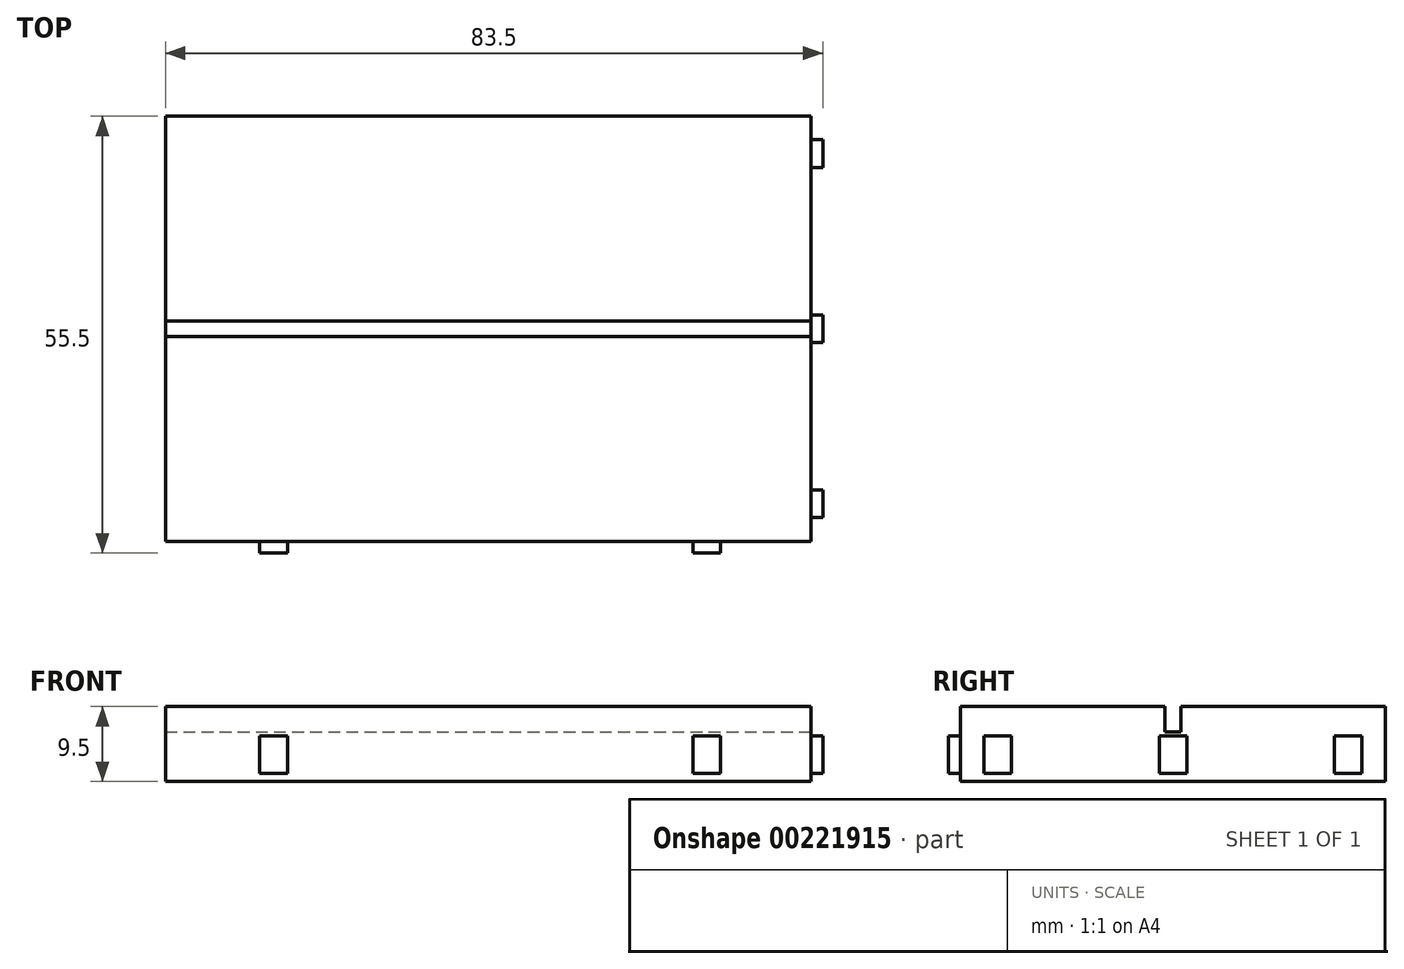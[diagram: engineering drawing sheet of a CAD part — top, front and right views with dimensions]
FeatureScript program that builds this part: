
annotation { "Feature Type Name" : "Feature", "Feature Type Description" : "" }
export const myFeature = defineFeature(function(context is Context, id is Id, definition is map)
    precondition{}
    {
        {
            var Q0;
            Q0=qCreatedBy(makeId("Top.planeOp"),FACE);
            var sketch = newSketch(context, id + "F0", { "sketchPlane" : qUnion([Q0])});
            skLineSegment(sketch, "E0.bottom", {"start": v(41, -27) * mm, "end": v(-41, -27) * mm});
            skLineSegment(sketch, "E0.top", {"start": v(41, 27) * mm, "end": v(-41, 27) * mm});
            skLineSegment(sketch, "E0.left", {"start": v(41, -27) * mm, "end": v(41, 27) * mm});
            skLineSegment(sketch, "E0.right", {"start": v(-41, -27) * mm, "end": v(-41, 27) * mm});
            skPoint(sketch, "E0.middle", {"position": v(0, 0) * mm});
            skSolve(sketch);
        }
        {
            var Q0;
            Q0=makeQuery(id+"F0.imprint","IMPRINT",FACE,{"disambiguationData":[TD([[makeQuery(id+"F0.imprint","IMPRINT",EDGE,{"derivedFrom":sQuery(id+"F0.wireOp",EDGE,"E0.bottom")}),-1.0]])]});
            extrude(context, id + "F1", {"entities" : qUnion([Q0]), "depth" : 9.5 * mm});
        }
        {
            var Q0;
            Q0=makeQuery(id+"F1.opExtrude","CAP_FACE",FACE,{"disambiguationData":[OSD([sQuery(id+"F0.wireOp",EDGE,"E0.bottom"),sQuery(id+"F0.wireOp",EDGE,"E0.top"),sQuery(id+"F0.wireOp",EDGE,"E0.left"),sQuery(id+"F0.wireOp",EDGE,"E0.right")])],"isStart":false});
            var sketch = newSketch(context, id + "F2", { "sketchPlane" : qUnion([Q0])});
            skLineSegment(sketch, "E1.bottom", {"start": v(-41, 1) * mm, "end": v(41, 1) * mm});
            skLineSegment(sketch, "E1.top", {"start": v(-41, -1) * mm, "end": v(41, -1) * mm});
            skLineSegment(sketch, "E1.left", {"start": v(-41, 1) * mm, "end": v(-41, -1) * mm});
            skLineSegment(sketch, "E1.right", {"start": v(41, 1) * mm, "end": v(41, -1) * mm});
            skPoint(sketch, "E1.middle", {"position": v(0, 0) * mm});
            skSolve(sketch);
        }
        {
            var Q0;
            Q0=makeQuery(id+"F2.imprint","IMPRINT",FACE,{"disambiguationData":[TD([[makeQuery(id+"F2.imprint","IMPRINT",EDGE,{"derivedFrom":sQuery(id+"F2.wireOp",EDGE,"E1.bottom")}),-1.0]])]});
            extrude(context, id + "F3", {"entities" : qUnion([Q0]), "operationType" : NewBodyOperationType.REMOVE, "oppositeDirection" : true, "depth" : 3.2 * mm});
        }
        {
            var Q0;
            Q0=makeQuery(id+"F1.opExtrude","SWEPT_FACE",FACE,{"disambiguationData":[OSD([sQuery(id+"F0.wireOp",EDGE,"E0.bottom")])]});
            var sketch = newSketch(context, id + "F4", { "sketchPlane" : qUnion([Q0])});
            skLineSegment(sketch, "E2.bottom", {"start": v(-29, 5.8) * mm, "end": v(-25.5, 5.8) * mm});
            skLineSegment(sketch, "E2.top", {"start": v(-29, 1) * mm, "end": v(-25.5, 1) * mm});
            skLineSegment(sketch, "E2.left", {"start": v(-29, 5.8) * mm, "end": v(-29, 1) * mm});
            skLineSegment(sketch, "E2.right", {"start": v(-25.5, 5.8) * mm, "end": v(-25.5, 1) * mm});
            skLineSegment(sketch, "E3.bottom", {"start": v(26, 5.8) * mm, "end": v(29.5, 5.8) * mm});
            skLineSegment(sketch, "E3.top", {"start": v(26, 1) * mm, "end": v(29.5, 1) * mm});
            skLineSegment(sketch, "E3.left", {"start": v(26, 5.8) * mm, "end": v(26, 1) * mm});
            skLineSegment(sketch, "E3.right", {"start": v(29.5, 5.8) * mm, "end": v(29.5, 1) * mm});
            skLineSegment(sketch, "E4", {"start": v(-27.25, 1) * mm, "end": v(-27.25, 0) * mm, "construction": true});
            skSolve(sketch);
        }
        {
            var Q0;
            Q0=makeQuery(id+"F1.opExtrude","SWEPT_FACE",FACE,{"disambiguationData":[OSD([sQuery(id+"F0.wireOp",EDGE,"E0.left")])]});
            var sketch = newSketch(context, id + "F5", { "sketchPlane" : qUnion([Q0])});
            skLineSegment(sketch, "E5.bottom", {"start": v(-24, 5.8) * mm, "end": v(-20.5, 5.8) * mm});
            skLineSegment(sketch, "E5.top", {"start": v(-24, 1) * mm, "end": v(-20.5, 1) * mm});
            skLineSegment(sketch, "E5.left", {"start": v(-24, 5.8) * mm, "end": v(-24, 1) * mm});
            skLineSegment(sketch, "E5.right", {"start": v(-20.5, 5.8) * mm, "end": v(-20.5, 1) * mm});
            skLineSegment(sketch, "E6.bottom", {"start": v(-1.75, 5.8) * mm, "end": v(1.75, 5.8) * mm});
            skLineSegment(sketch, "E6.top", {"start": v(-1.75, 1) * mm, "end": v(1.75, 1) * mm});
            skLineSegment(sketch, "E6.left", {"start": v(-1.75, 5.8) * mm, "end": v(-1.75, 1) * mm});
            skLineSegment(sketch, "E6.right", {"start": v(1.75, 5.8) * mm, "end": v(1.75, 1) * mm});
            skLineSegment(sketch, "E7.bottom", {"start": v(20.5, 5.8) * mm, "end": v(24, 5.8) * mm});
            skLineSegment(sketch, "E7.top", {"start": v(20.5, 1) * mm, "end": v(24, 1) * mm});
            skLineSegment(sketch, "E7.left", {"start": v(20.5, 5.8) * mm, "end": v(20.5, 1) * mm});
            skLineSegment(sketch, "E7.right", {"start": v(24, 5.8) * mm, "end": v(24, 1) * mm});
            skLineSegment(sketch, "E8", {"start": v(-14, 9.5) * mm, "end": v(0, 0) * mm, "construction": true});
            skPoint(sketch, "E9", {"position": v(0, 5.8) * mm});
            skSolve(sketch);
        }
        {
            var Q0;
            Q0=makeQuery(id+"F4.imprint","IMPRINT",FACE,{"disambiguationData":[TD([[makeQuery(id+"F4.imprint","IMPRINT",EDGE,{"derivedFrom":sQuery(id+"F4.wireOp",EDGE,"E3.bottom")}),-1.0]])]});
            var Q1;
            Q1=makeQuery(id+"F4.imprint","IMPRINT",FACE,{"disambiguationData":[TD([[makeQuery(id+"F4.imprint","IMPRINT",EDGE,{"derivedFrom":sQuery(id+"F4.wireOp",EDGE,"E2.bottom")}),-1.0]])]});
            extrude(context, id + "F6", {"entities" : qUnion([Q0, Q1]), "operationType" : NewBodyOperationType.ADD, "depth" : 1.5 * mm});
        }
        {
            var Q0;
            Q0=makeQuery(id+"F5.imprint","IMPRINT",FACE,{"disambiguationData":[TD([[makeQuery(id+"F5.imprint","IMPRINT",EDGE,{"derivedFrom":sQuery(id+"F5.wireOp",EDGE,"E5.bottom")}),-1.0]])]});
            var Q1;
            Q1=makeQuery(id+"F5.imprint","IMPRINT",FACE,{"disambiguationData":[TD([[makeQuery(id+"F5.imprint","IMPRINT",EDGE,{"derivedFrom":sQuery(id+"F5.wireOp",EDGE,"E6.bottom")}),-1.0]])]});
            var Q2;
            Q2=makeQuery(id+"F5.imprint","IMPRINT",FACE,{"disambiguationData":[TD([[makeQuery(id+"F5.imprint","IMPRINT",EDGE,{"derivedFrom":sQuery(id+"F5.wireOp",EDGE,"E7.bottom")}),-1.0]])]});
            extrude(context, id + "F7", {"entities" : qUnion([Q0, Q1, Q2]), "operationType" : NewBodyOperationType.ADD, "depth" : 1.5 * mm});
        }
    });
